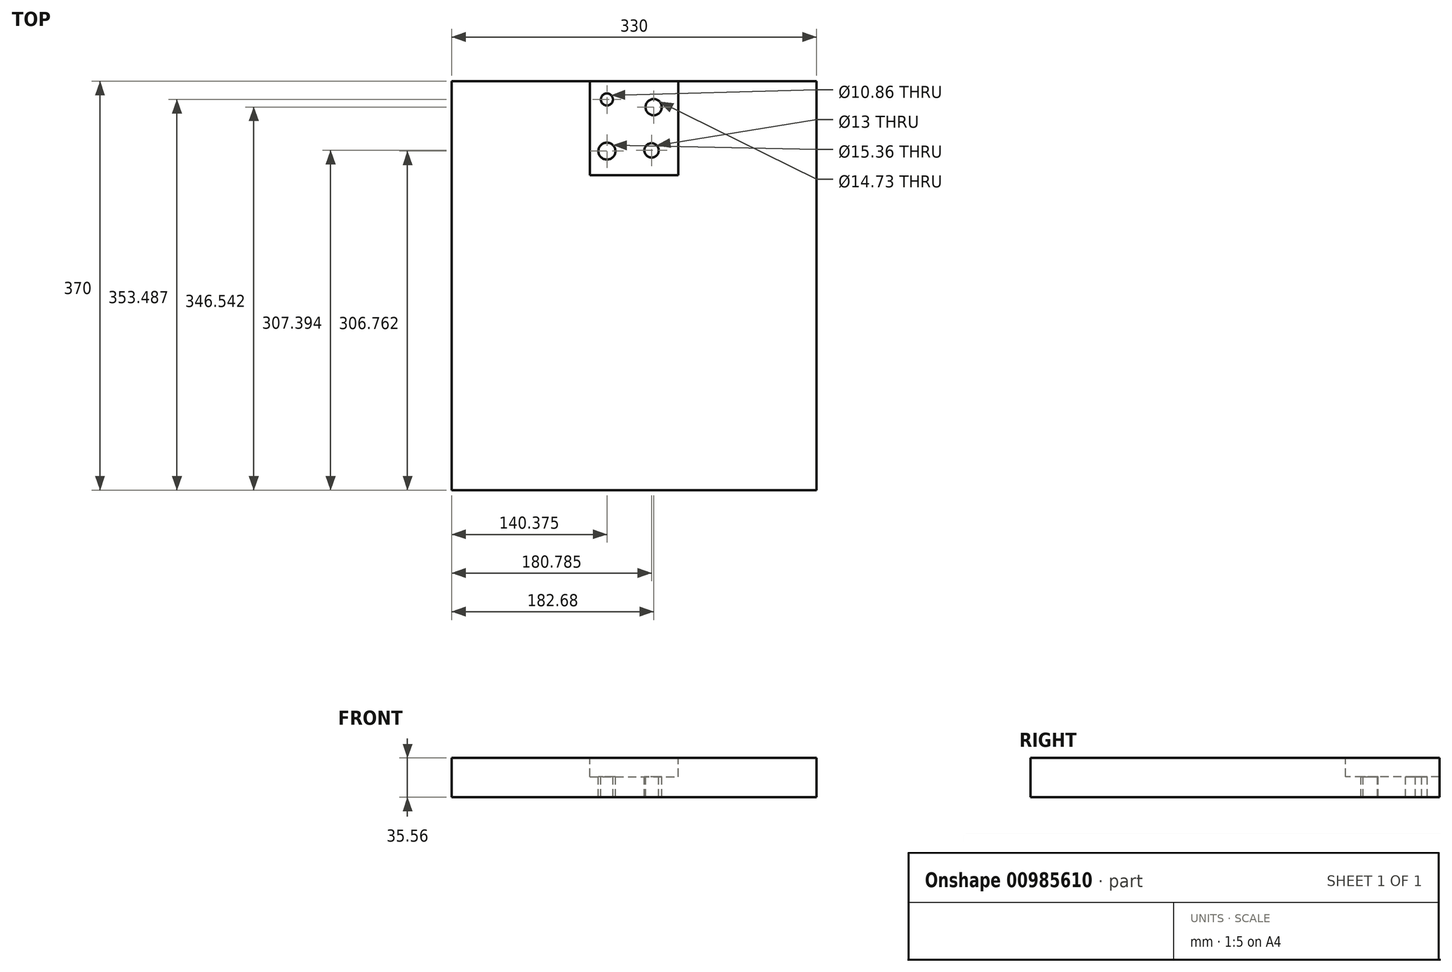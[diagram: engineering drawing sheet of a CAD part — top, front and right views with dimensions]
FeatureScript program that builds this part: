
annotation { "Feature Type Name" : "Feature", "Feature Type Description" : "" }
export const myFeature = defineFeature(function(context is Context, id is Id, definition is map)
    precondition{}
    {
        {
            var Q0;
            Q0=qCreatedBy(makeId("Top.planeOp"),FACE);
            var sketch = newSketch(context, id + "F0", { "sketchPlane" : qUnion([Q0])});
            skLineSegment(sketch, "E0.bottom", {"start": v(-165, 0) * mm, "end": v(165, 0) * mm});
            skLineSegment(sketch, "E0.top", {"start": v(-165, -370) * mm, "end": v(165, -370) * mm});
            skLineSegment(sketch, "E0.left", {"start": v(-165, 0) * mm, "end": v(-165, -370) * mm});
            skLineSegment(sketch, "E0.right", {"start": v(165, 0) * mm, "end": v(165, -370) * mm});
            skSolve(sketch);
        }
        {
            var Q0;
            Q0 = qSketchRegion(id + "F0", true);
            extrude(context, id + "F1", {"entities" : qUnion([Q0]), "depth" : 35.56 * mm, "offsetDistance" : 25.4 * mm});
        }
        {
            var Q0;
            Q0=makeQuery(id+"F1.opExtrude","CAP_FACE",FACE,{"disambiguationData":[OSD([sQuery(id+"F0.wireOp",EDGE,"E0.bottom"),sQuery(id+"F0.wireOp",EDGE,"E0.top"),sQuery(id+"F0.wireOp",EDGE,"E0.left"),sQuery(id+"F0.wireOp",EDGE,"E0.right")])],"isStart":false});
            var sketch = newSketch(context, id + "F2", { "sketchPlane" : qUnion([Q0])});
            skLineSegment(sketch, "E1.bottom", {"start": v(-40, 0) * mm, "end": v(40, 0) * mm});
            skLineSegment(sketch, "E1.top", {"start": v(-40, -85) * mm, "end": v(40, -85) * mm});
            skLineSegment(sketch, "E1.left", {"start": v(-40, 0) * mm, "end": v(-40, -85) * mm});
            skLineSegment(sketch, "E1.right", {"start": v(40, 0) * mm, "end": v(40, -85) * mm});
            skSolve(sketch);
        }
        {
            var Q0;
            Q0 = qSketchRegion(id + "F2", true);
            extrude(context, id + "F3", {"entities" : qUnion([Q0]), "operationType" : NewBodyOperationType.REMOVE, "oppositeDirection" : true, "depth" : 17 * mm, "offsetDistance" : 25.4 * mm});
        }
        {
            var Q0;
            Q0=makeQuery(id+"F3.boolean.opBoolean","COPY",FACE,{"derivedFrom":makeQuery(id+"F3.opExtrude","CAP_FACE",FACE,{"disambiguationData":[OSD([sQuery(id+"F2.wireOp",EDGE,"E1.bottom"),sQuery(id+"F2.wireOp",EDGE,"E1.top"),sQuery(id+"F2.wireOp",EDGE,"E1.left"),sQuery(id+"F2.wireOp",EDGE,"E1.right")])],"isStart":false})});
            var sketch = newSketch(context, id + "F4", { "sketchPlane" : qUnion([Q0])});
            skCircle(sketch, "E2", {"center": v(-24.63, -16.51) * mm, "radius": 5.43 * mm});
            skCircle(sketch, "E3", {"center": v(17.68, -23.46) * mm, "radius": 7.36 * mm});
            skCircle(sketch, "E4", {"center": v(-24.63, -63.24) * mm, "radius": 7.68 * mm});
            skCircle(sketch, "E5", {"center": v(15.79, -62.6) * mm, "radius": 6.5 * mm});
            skSolve(sketch);
        }
        {
            var Q0;
            Q0 = qSketchRegion(id + "F4", true);
            extrude(context, id + "F5", {"entities" : qUnion([Q0]), "operationType" : NewBodyOperationType.REMOVE, "endBound" : BoundingType.THROUGH_ALL, "oppositeDirection" : true, "depth" : 25.4 * mm, "offsetDistance" : 25.4 * mm});
        }
    });
